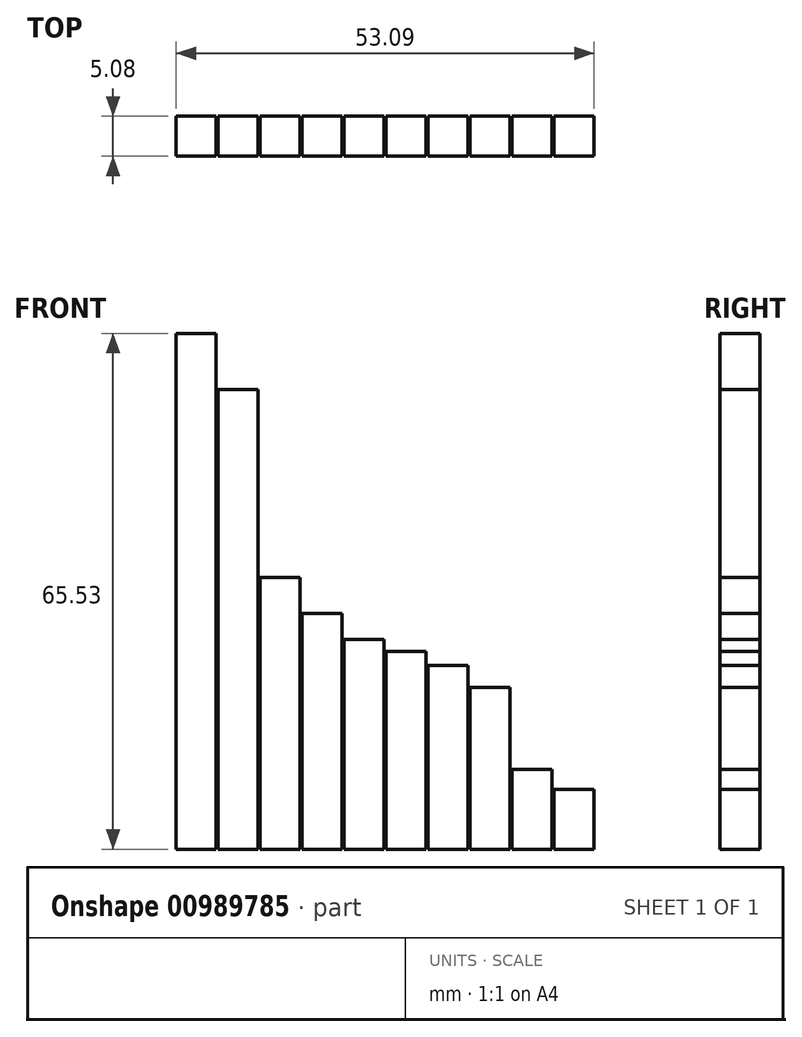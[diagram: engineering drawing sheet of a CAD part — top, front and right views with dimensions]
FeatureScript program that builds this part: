
annotation { "Feature Type Name" : "Feature", "Feature Type Description" : "" }
export const myFeature = defineFeature(function(context is Context, id is Id, definition is map)
    precondition{}
    {
        {
            var Q0;
            Q0=qCreatedBy(makeId("Top.planeOp"),FACE);
            var sketch = newSketch(context, id + "F0", { "sketchPlane" : qUnion([Q0])});
            skLineSegment(sketch, "E0.bottom", {"start": v(0, 0) * mm, "end": v(5.08, 0) * mm});
            skLineSegment(sketch, "E0.top", {"start": v(0, -5.08) * mm, "end": v(5.08, -5.08) * mm});
            skLineSegment(sketch, "E0.left", {"start": v(0, 0) * mm, "end": v(0, -5.08) * mm});
            skLineSegment(sketch, "E0.right", {"start": v(5.08, 0) * mm, "end": v(5.08, -5.08) * mm});
            skSolve(sketch);
        }
        {
            var Q0;
            Q0=qCreatedBy(makeId("Top.planeOp"),FACE);
            var sketch = newSketch(context, id + "F1", { "sketchPlane" : qUnion([Q0])});
            skLineSegment(sketch, "E1.0.0", {"start": v(0, 0) * mm, "end": v(0, -5.08) * mm});
            skLineSegment(sketch, "E1.0.1", {"start": v(0, -5.08) * mm, "end": v(5.08, -5.08) * mm});
            skLineSegment(sketch, "E1.0.2", {"start": v(5.08, -5.08) * mm, "end": v(5.08, 0) * mm});
            skLineSegment(sketch, "E1.0.3", {"start": v(5.08, 0) * mm, "end": v(0, 0) * mm});
            skLineSegment(sketch, "E2.1.0.0", {"start": v(10.41, 0) * mm, "end": v(5.33, 0) * mm});
            skLineSegment(sketch, "E2.1.0.1", {"start": v(5.33, -5.08) * mm, "end": v(10.41, -5.08) * mm});
            skLineSegment(sketch, "E2.1.0.2", {"start": v(5.33, 0) * mm, "end": v(5.33, -5.08) * mm});
            skLineSegment(sketch, "E2.1.0.3", {"start": v(10.41, -5.08) * mm, "end": v(10.41, 0) * mm});
            skLineSegment(sketch, "E2.2.0.0", {"start": v(15.75, 0) * mm, "end": v(10.67, 0) * mm});
            skLineSegment(sketch, "E2.2.0.1", {"start": v(10.67, -5.08) * mm, "end": v(15.75, -5.08) * mm});
            skLineSegment(sketch, "E2.2.0.2", {"start": v(10.67, 0) * mm, "end": v(10.67, -5.08) * mm});
            skLineSegment(sketch, "E2.2.0.3", {"start": v(15.75, -5.08) * mm, "end": v(15.75, 0) * mm});
            skLineSegment(sketch, "E2.3.0.0", {"start": v(21.08, 0) * mm, "end": v(16, 0) * mm});
            skLineSegment(sketch, "E2.3.0.1", {"start": v(16, -5.08) * mm, "end": v(21.08, -5.08) * mm});
            skLineSegment(sketch, "E2.3.0.2", {"start": v(16, 0) * mm, "end": v(16, -5.08) * mm});
            skLineSegment(sketch, "E2.3.0.3", {"start": v(21.08, -5.08) * mm, "end": v(21.08, 0) * mm});
            skLineSegment(sketch, "E2.4.0.0", {"start": v(26.42, 0) * mm, "end": v(21.34, 0) * mm});
            skLineSegment(sketch, "E2.4.0.1", {"start": v(21.34, -5.08) * mm, "end": v(26.42, -5.08) * mm});
            skLineSegment(sketch, "E2.4.0.2", {"start": v(21.34, 0) * mm, "end": v(21.34, -5.08) * mm});
            skLineSegment(sketch, "E2.4.0.3", {"start": v(26.42, -5.08) * mm, "end": v(26.42, 0) * mm});
            skLineSegment(sketch, "E2.5.0.0", {"start": v(31.75, 0) * mm, "end": v(26.67, 0) * mm});
            skLineSegment(sketch, "E2.5.0.1", {"start": v(26.67, -5.08) * mm, "end": v(31.75, -5.08) * mm});
            skLineSegment(sketch, "E2.5.0.2", {"start": v(26.67, 0) * mm, "end": v(26.67, -5.08) * mm});
            skLineSegment(sketch, "E2.5.0.3", {"start": v(31.75, -5.08) * mm, "end": v(31.75, 0) * mm});
            skLineSegment(sketch, "E2.6.0.0", {"start": v(37.08, 0) * mm, "end": v(32, 0) * mm});
            skLineSegment(sketch, "E2.6.0.1", {"start": v(32, -5.08) * mm, "end": v(37.08, -5.08) * mm});
            skLineSegment(sketch, "E2.6.0.2", {"start": v(32, 0) * mm, "end": v(32, -5.08) * mm});
            skLineSegment(sketch, "E2.6.0.3", {"start": v(37.08, -5.08) * mm, "end": v(37.08, 0) * mm});
            skLineSegment(sketch, "E2.7.0.0", {"start": v(42.42, 0) * mm, "end": v(37.34, 0) * mm});
            skLineSegment(sketch, "E2.7.0.1", {"start": v(37.34, -5.08) * mm, "end": v(42.42, -5.08) * mm});
            skLineSegment(sketch, "E2.7.0.2", {"start": v(37.34, 0) * mm, "end": v(37.34, -5.08) * mm});
            skLineSegment(sketch, "E2.7.0.3", {"start": v(42.42, -5.08) * mm, "end": v(42.42, 0) * mm});
            skLineSegment(sketch, "E2.8.0.0", {"start": v(47.75, 0) * mm, "end": v(42.67, 0) * mm});
            skLineSegment(sketch, "E2.8.0.1", {"start": v(42.67, -5.08) * mm, "end": v(47.75, -5.08) * mm});
            skLineSegment(sketch, "E2.8.0.2", {"start": v(42.67, 0) * mm, "end": v(42.67, -5.08) * mm});
            skLineSegment(sketch, "E2.8.0.3", {"start": v(47.75, -5.08) * mm, "end": v(47.75, 0) * mm});
            skLineSegment(sketch, "E2.9.0.0", {"start": v(53.09, 0) * mm, "end": v(48, 0) * mm});
            skLineSegment(sketch, "E2.9.0.1", {"start": v(48, -5.08) * mm, "end": v(53.09, -5.08) * mm});
            skLineSegment(sketch, "E2.9.0.2", {"start": v(48, 0) * mm, "end": v(48, -5.08) * mm});
            skLineSegment(sketch, "E2.9.0.3", {"start": v(53.09, -5.08) * mm, "end": v(53.09, 0) * mm});
            skLineSegment(sketch, "E2.direction1", {"start": v(0, -5.08) * mm, "end": v(5.33, -5.08) * mm, "construction": true});
            skSolve(sketch);
        }
        {
            var Q0;
            Q0=makeQuery(id+"F0.imprint","IMPRINT",FACE,{"disambiguationData":[TD([[makeQuery(id+"F0.imprint","IMPRINT",EDGE,{"derivedFrom":sQuery(id+"F0.wireOp",EDGE,"E0.bottom")}),-1.0]])]});
            extrude(context, id + "F2", {"entities" : qUnion([Q0]), "depth" : 65.53 * mm, "offsetDistance" : 25.4 * mm});
        }
        {
            var Q0;
            Q0=makeQuery(id+"F1.imprint","IMPRINT",FACE,{"disambiguationData":[TD([[makeQuery(id+"F1.imprint","IMPRINT",EDGE,{"derivedFrom":sQuery(id+"F1.wireOp",EDGE,"E2.1.0.0")}),1.0]])]});
            extrude(context, id + "F3", {"entities" : qUnion([Q0]), "depth" : 58.42 * mm, "offsetDistance" : 25.4 * mm});
        }
        {
            var Q0;
            Q0=makeQuery(id+"F1.imprint","IMPRINT",FACE,{"disambiguationData":[TD([[makeQuery(id+"F1.imprint","IMPRINT",EDGE,{"derivedFrom":sQuery(id+"F1.wireOp",EDGE,"E2.2.0.0")}),1.0]])]});
            extrude(context, id + "F4", {"entities" : qUnion([Q0]), "depth" : 34.54 * mm, "offsetDistance" : 25.4 * mm});
        }
        {
            var Q0;
            Q0=makeQuery(id+"F1.imprint","IMPRINT",FACE,{"disambiguationData":[TD([[makeQuery(id+"F1.imprint","IMPRINT",EDGE,{"derivedFrom":sQuery(id+"F1.wireOp",EDGE,"E2.3.0.0")}),1.0]])]});
            extrude(context, id + "F5", {"entities" : qUnion([Q0]), "depth" : 29.97 * mm, "offsetDistance" : 25.4 * mm});
        }
        {
            var Q0;
            Q0=makeQuery(id+"F1.imprint","IMPRINT",FACE,{"disambiguationData":[TD([[makeQuery(id+"F1.imprint","IMPRINT",EDGE,{"derivedFrom":sQuery(id+"F1.wireOp",EDGE,"E2.4.0.0")}),1.0]])]});
            extrude(context, id + "F6", {"entities" : qUnion([Q0]), "depth" : 26.67 * mm, "offsetDistance" : 25.4 * mm});
        }
        {
            var Q0;
            Q0=makeQuery(id+"F1.imprint","IMPRINT",FACE,{"disambiguationData":[TD([[makeQuery(id+"F1.imprint","IMPRINT",EDGE,{"derivedFrom":sQuery(id+"F1.wireOp",EDGE,"E2.5.0.0")}),1.0]])]});
            extrude(context, id + "F7", {"entities" : qUnion([Q0]), "depth" : 25.15 * mm, "offsetDistance" : 25.4 * mm});
        }
        {
            var Q0;
            Q0=makeQuery(id+"F1.imprint","IMPRINT",FACE,{"disambiguationData":[TD([[makeQuery(id+"F1.imprint","IMPRINT",EDGE,{"derivedFrom":sQuery(id+"F1.wireOp",EDGE,"E2.6.0.0")}),1.0]])]});
            extrude(context, id + "F8", {"entities" : qUnion([Q0]), "depth" : 23.37 * mm, "offsetDistance" : 25.4 * mm});
        }
        {
            var Q0;
            Q0=makeQuery(id+"F1.imprint","IMPRINT",FACE,{"disambiguationData":[TD([[makeQuery(id+"F1.imprint","IMPRINT",EDGE,{"derivedFrom":sQuery(id+"F1.wireOp",EDGE,"E2.7.0.0")}),1.0]])]});
            extrude(context, id + "F9", {"entities" : qUnion([Q0]), "depth" : 20.57 * mm, "offsetDistance" : 25.4 * mm});
        }
        {
            var Q0;
            Q0=makeQuery(id+"F1.imprint","IMPRINT",FACE,{"disambiguationData":[TD([[makeQuery(id+"F1.imprint","IMPRINT",EDGE,{"derivedFrom":sQuery(id+"F1.wireOp",EDGE,"E2.8.0.0")}),1.0]])]});
            extrude(context, id + "F10", {"entities" : qUnion([Q0]), "depth" : 10.16 * mm, "offsetDistance" : 25.4 * mm});
        }
        {
            var Q0;
            Q0=makeQuery(id+"F1.imprint","IMPRINT",FACE,{"disambiguationData":[TD([[makeQuery(id+"F1.imprint","IMPRINT",EDGE,{"derivedFrom":sQuery(id+"F1.wireOp",EDGE,"E2.9.0.0")}),1.0]])]});
            extrude(context, id + "F11", {"entities" : qUnion([Q0]), "depth" : 7.62 * mm, "offsetDistance" : 25.4 * mm});
        }
    });
